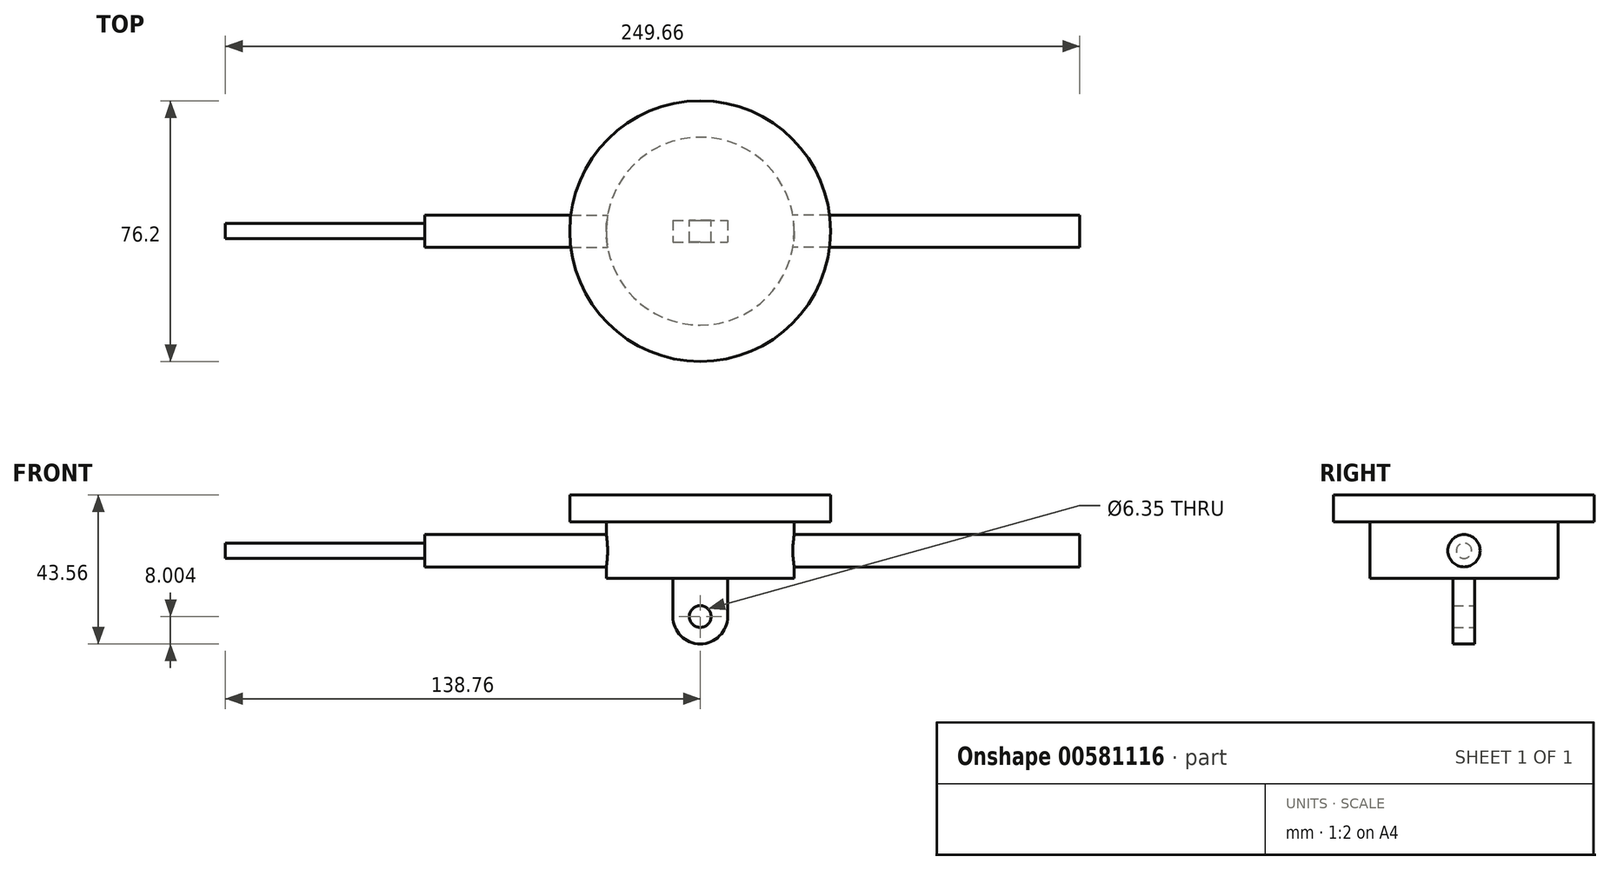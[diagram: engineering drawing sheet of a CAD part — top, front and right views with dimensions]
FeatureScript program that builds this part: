
annotation { "Feature Type Name" : "Feature", "Feature Type Description" : "" }
export const myFeature = defineFeature(function(context is Context, id is Id, definition is map)
    precondition{}
    {
        {
            var Q0;
            Q0=qCreatedBy(makeId("Top.planeOp"),FACE);
            var sketch = newSketch(context, id + "F0", { "sketchPlane" : qUnion([Q0])});
            skCircle(sketch, "E0", {"center": v(0, 0) * mm, "radius": 38.1 * mm});
            skSolve(sketch);
        }
        {
            var Q0;
            Q0=makeQuery(id+"F0.imprint","IMPRINT",FACE,{"disambiguationData":[TD([[makeQuery(id+"F0.imprint","IMPRINT",EDGE,{"derivedFrom":sQuery(id+"F0.wireOp",EDGE,"E0")}),1.0]])]});
            extrude(context, id + "F1", {"entities" : qUnion([Q0]), "depth" : 7.87 * mm, "offsetDistance" : 25.4 * mm});
        }
        {
            var Q0;
            Q0=qCreatedBy(makeId("Top.planeOp"),FACE);
            var sketch = newSketch(context, id + "F2", { "sketchPlane" : qUnion([Q0])});
            skCircle(sketch, "E1", {"center": v(0, 0) * mm, "radius": 27.47 * mm});
            skSolve(sketch);
        }
        {
            var Q0;
            Q0=makeQuery(id+"F2.imprint","IMPRINT",FACE,{"disambiguationData":[TD([[makeQuery(id+"F2.imprint","IMPRINT",EDGE,{"derivedFrom":sQuery(id+"F2.wireOp",EDGE,"E1")}),1.0]])]});
            extrude(context, id + "F3", {"entities" : qUnion([Q0]), "operationType" : NewBodyOperationType.ADD, "oppositeDirection" : true, "depth" : 16.5 * mm, "offsetDistance" : 25.4 * mm});
        }
        {
            var Q0;
            Q0=qCreatedBy(makeId("Right.planeOp"),FACE);
            var sketch = newSketch(context, id + "F4", { "sketchPlane" : qUnion([Q0])});
            skCircle(sketch, "E2", {"center": v(0, -8.43) * mm, "radius": 4.72 * mm});
            skSolve(sketch);
        }
        {
            var Q0;
            Q0 = qSketchRegion(id + "F4", true);
            extrude(context, id + "F5", {"entities" : qUnion([Q0]), "operationType" : NewBodyOperationType.ADD, "depth" : 110.9 * mm, "offsetDistance" : 25.4 * mm});
        }
        {
            var Q0;
            Q0 = qSketchRegion(id + "F4", true);
            extrude(context, id + "F6", {"entities" : qUnion([Q0]), "operationType" : NewBodyOperationType.ADD, "oppositeDirection" : true, "depth" : 80.47 * mm, "offsetDistance" : 25.4 * mm});
        }
        {
            var Q0;
            Q0=makeQuery(id+"F6.opExtrude","CAP_FACE",FACE,{"disambiguationData":[OSD([sQuery(id+"F4.wireOp",EDGE,"E2")])],"isStart":false});
            var sketch = newSketch(context, id + "F7", { "sketchPlane" : qUnion([Q0])});
            skCircle(sketch, "E3", {"center": v(0, -8.43) * mm, "radius": 2.24 * mm});
            skSolve(sketch);
        }
        {
            var Q0;
            Q0 = qSketchRegion(id + "F7", true);
            extrude(context, id + "F8", {"entities" : qUnion([Q0]), "operationType" : NewBodyOperationType.ADD, "depth" : 58.3 * mm, "offsetDistance" : 25.4 * mm});
        }
        {
            var Q0;
            Q0=makeQuery(id+"F3.opExtrude","CAP_FACE",FACE,{"disambiguationData":[OSD([sQuery(id+"F2.wireOp",EDGE,"E1")])],"isStart":false});
            var sketch = newSketch(context, id + "F9", { "sketchPlane" : qUnion([Q0])});
            skLineSegment(sketch, "E4.bottom", {"start": v(-8, -3.17) * mm, "end": v(8, -3.17) * mm});
            skLineSegment(sketch, "E4.top", {"start": v(-8, 3.18) * mm, "end": v(8, 3.18) * mm});
            skLineSegment(sketch, "E4.left", {"start": v(-8, -3.17) * mm, "end": v(-8, 3.18) * mm});
            skLineSegment(sketch, "E4.right", {"start": v(8, -3.17) * mm, "end": v(8, 3.18) * mm});
            skPoint(sketch, "E4.middle", {"position": v(0, 0) * mm});
            skSolve(sketch);
        }
        {
            var Q0;
            Q0 = qSketchRegion(id + "F9", true);
            extrude(context, id + "F10", {"entities" : qUnion([Q0]), "operationType" : NewBodyOperationType.ADD, "depth" : 19.18 * mm, "offsetDistance" : 25.4 * mm});
        }
        {
            var Q0;
            Q0=makeQuery(id+"F10.opExtrude","CAP_EDGE",EDGE,{"disambiguationData":[OSD([sQuery(id+"F9.wireOp",EDGE,"E4.right")])],"isStart":false});
            var Q1;
            Q1=makeQuery(id+"F10.opExtrude","CAP_EDGE",EDGE,{"disambiguationData":[OSD([sQuery(id+"F9.wireOp",EDGE,"E4.left")])],"isStart":false});
            fillet(context, id + "F11", {"entities" : qUnion([Q0, Q1]), "radius" : 8 * mm, "tangentPropagation" : true, "allowEdgeOverflow" : false});
        }
        {
            var Q0;
            Q0=makeQuery(id+"F10.opExtrude","SWEPT_FACE",FACE,{"disambiguationData":[OSD([sQuery(id+"F9.wireOp",EDGE,"E4.bottom")])]});
            var sketch = newSketch(context, id + "F12", { "sketchPlane" : qUnion([Q0])});
            skPoint(sketch, "E5", {"position": v(0, -27.69) * mm});
            skSolve(sketch);
        }
        {
            var Q0;
            Q0=sQuery(id+"F12.wireOp",VERTEX,"E5");
            var Q1;
            Q1=makeQuery(id+"F1.opExtrude","SWEPT_BODY",BODY,{"disambiguationData":[OSD([sQuery(id+"F0.wireOp",EDGE,"E0")])]});
            hole(context, id + "F13", {"style" : HoleStyle.SIMPLE, "endStyle" : HoleEndStyle.THROUGH, "holeDiameter" : 6.35 * mm, "majorDiameter" : 6.35 * mm, "isTappedThrough" : true, "tappedDepth" : 12.7 * mm, "tapClearance" : 3, "locations" : qUnion([Q0]), "scope" : qUnion([Q1])});
        }
    });
